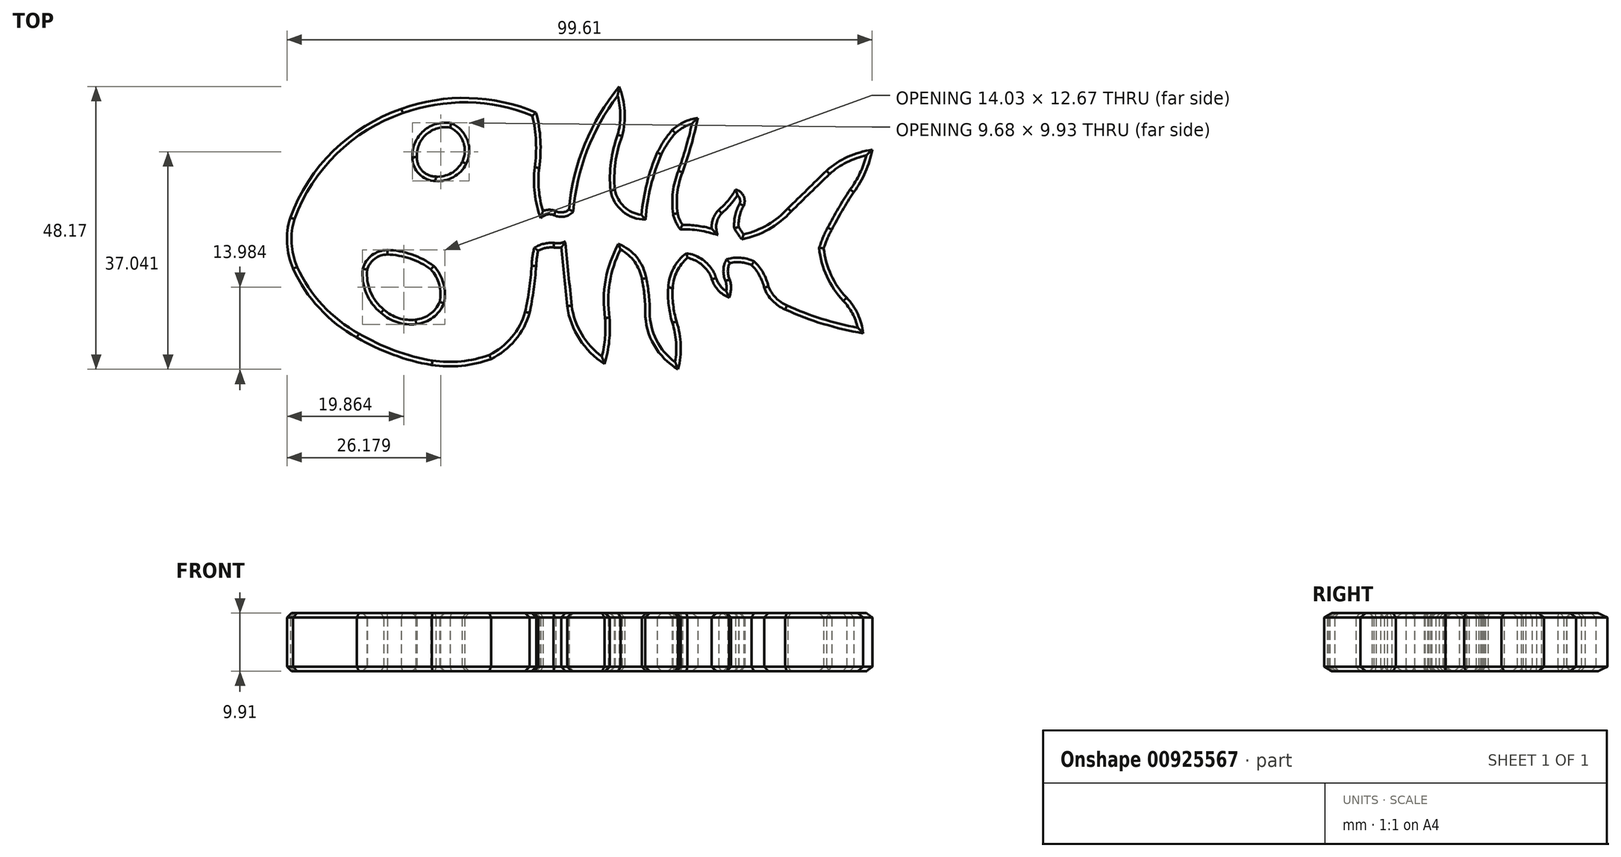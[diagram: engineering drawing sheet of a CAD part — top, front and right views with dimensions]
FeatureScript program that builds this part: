
annotation { "Feature Type Name" : "Feature", "Feature Type Description" : "" }
export const myFeature = defineFeature(function(context is Context, id is Id, definition is map)
    precondition{}
    {
        {
            var Q0;
            Q0=qCreatedBy(makeId("Top.planeOp"),FACE);
            var sketch = newSketch(context, id + "F0", { "sketchPlane" : qUnion([Q0])});
            skArc(sketch, "E0", {"start": v(-60.04, 23.84) * mm, "mid": v(-71.6, 16.74) * mm, "end": v(-78.96, 5.34) * mm});
            skArc(sketch, "E1", {"start": v(-37.1, 23.22) * mm, "mid": v(-48.52, 25.7) * mm, "end": v(-60.04, 23.84) * mm});
            skArc(sketch, "E2", {"start": v(-36.6, 13.8) * mm, "mid": v(-36.38, 18.53) * mm, "end": v(-37.1, 23.22) * mm});
            skArc(sketch, "E3", {"start": v(-36.6, 13.8) * mm, "mid": v(-36.65, 10.08) * mm, "end": v(-35.92, 6.44) * mm});
            skArc(sketch, "E4", {"start": v(-33.76, 6.44) * mm, "mid": v(-34.84, 6.66) * mm, "end": v(-35.92, 6.44) * mm});
            skArc(sketch, "E5", {"start": v(-33.76, 6.44) * mm, "mid": v(-32.6, 6.23) * mm, "end": v(-31.52, 6.72) * mm});
            skArc(sketch, "E6", {"start": v(-22.96, 27.66) * mm, "mid": v(-28.83, 17.84) * mm, "end": v(-31.52, 6.72) * mm});
            skArc(sketch, "E7", {"start": v(-22.49, 19.2) * mm, "mid": v(-22.03, 23.47) * mm, "end": v(-22.96, 27.66) * mm});
            skArc(sketch, "E8", {"start": v(-22.49, 19.2) * mm, "mid": v(-23.6, 14.71) * mm, "end": v(-23.7, 10.08) * mm});
            skArc(sketch, "E9", {"start": v(-23.7, 10.08) * mm, "mid": v(-22.13, 7.2) * mm, "end": v(-19.16, 5.8) * mm});
            skArc(sketch, "E10", {"start": v(-16.47, 16.41) * mm, "mid": v(-18.25, 11.21) * mm, "end": v(-19.16, 5.8) * mm});
            skArc(sketch, "E11", {"start": v(-13.94, 20.27) * mm, "mid": v(-15.34, 18.43) * mm, "end": v(-16.47, 16.41) * mm});
            skArc(sketch, "E12", {"start": v(-9.6, 22.32) * mm, "mid": v(-11.92, 21.61) * mm, "end": v(-13.94, 20.27) * mm});
            skArc(sketch, "E13", {"start": v(-12.2, 13.03) * mm, "mid": v(-10.72, 17.63) * mm, "end": v(-9.6, 22.32) * mm});
            skArc(sketch, "E14", {"start": v(-12.2, 13.03) * mm, "mid": v(-13.06, 9.6) * mm, "end": v(-13.04, 6.06) * mm});
            skArc(sketch, "E15", {"start": v(-13.04, 6.06) * mm, "mid": v(-12.7, 5.05) * mm, "end": v(-12.2, 4.12) * mm});
            skArc(sketch, "E16", {"start": v(-7.21, 3.46) * mm, "mid": v(-9.68, 3.95) * mm, "end": v(-12.2, 4.12) * mm});
            skArc(sketch, "E17", {"start": v(-6.05, 6.63) * mm, "mid": v(-6.97, 5.17) * mm, "end": v(-7.21, 3.46) * mm});
            skArc(sketch, "E18", {"start": v(-6.05, 6.63) * mm, "mid": v(-4.45, 8.24) * mm, "end": v(-3.16, 10.11) * mm});
            skArc(sketch, "E19", {"start": v(-1.78, 7.35) * mm, "mid": v(-1.82, 9.06) * mm, "end": v(-3.16, 10.11) * mm});
            skArc(sketch, "E20", {"start": v(-1.78, 7.35) * mm, "mid": v(-2.47, 5.6) * mm, "end": v(-2.63, 3.74) * mm});
            skArc(sketch, "E21", {"start": v(-2.63, 3.74) * mm, "mid": v(-2.22, 3.1) * mm, "end": v(-1.78, 2.48) * mm});
            skArc(sketch, "E22", {"start": v(-1.78, 2.48) * mm, "mid": v(2.33, 4.12) * mm, "end": v(5.75, 6.91) * mm});
            skArc(sketch, "E23", {"start": v(12.32, 13.31) * mm, "mid": v(9.03, 10.11) * mm, "end": v(5.75, 6.91) * mm});
            skArc(sketch, "E24", {"start": v(20.1, 16.9) * mm, "mid": v(15.95, 15.68) * mm, "end": v(12.32, 13.31) * mm});
            skArc(sketch, "E25", {"start": v(16.96, 9.67) * mm, "mid": v(18.94, 13.1) * mm, "end": v(20.1, 16.9) * mm});
            skArc(sketch, "E26", {"start": v(16.96, 9.67) * mm, "mid": v(15, 6.52) * mm, "end": v(13.2, 3.27) * mm});
            skArc(sketch, "E27", {"start": v(13.2, 3.27) * mm, "mid": v(12.44, 1.72) * mm, "end": v(11.85, 0.1) * mm});
            skArc(sketch, "E28", {"start": v(-49.69, 14.84) * mm, "mid": v(-49.5, 18.2) * mm, "end": v(-51.76, 20.68) * mm});
            skArc(sketch, "E29", {"start": v(-51.76, 20.68) * mm, "mid": v(-55.8, 19.5) * mm, "end": v(-57.41, 15.62) * mm});
            skArc(sketch, "E30", {"start": v(-57.41, 15.62) * mm, "mid": v(-56.48, 13.3) * mm, "end": v(-54.18, 12.33) * mm});
            skArc(sketch, "E31", {"start": v(-54.18, 12.33) * mm, "mid": v(-51.55, 12.9) * mm, "end": v(-49.69, 14.84) * mm});
            skArc(sketch, "E32", {"start": v(-53.52, -9.03) * mm, "mid": v(-53.61, -6.08) * mm, "end": v(-55.03, -3.48) * mm});
            skArc(sketch, "E33", {"start": v(-57.6, -12.05) * mm, "mid": v(-55.15, -11.1) * mm, "end": v(-53.52, -9.03) * mm});
            skArc(sketch, "E34", {"start": v(-63.02, -10.32) * mm, "mid": v(-60.5, -11.78) * mm, "end": v(-57.6, -12.05) * mm});
            skArc(sketch, "E35", {"start": v(-65.86, -3.53) * mm, "mid": v(-65.3, -7.28) * mm, "end": v(-63.02, -10.32) * mm});
            skArc(sketch, "E36", {"start": v(-62.44, -0.95) * mm, "mid": v(-64.58, -1.68) * mm, "end": v(-65.86, -3.53) * mm});
            skArc(sketch, "E37", {"start": v(-55.03, -3.48) * mm, "mid": v(-58.54, -1.65) * mm, "end": v(-62.44, -0.95) * mm});
            skArc(sketch, "E38", {"start": v(-78.96, 5.34) * mm, "mid": v(-79.48, 0.94) * mm, "end": v(-78.46, -3.36) * mm});
            skArc(sketch, "E39", {"start": v(-78.46, -3.36) * mm, "mid": v(-74, -10.1) * mm, "end": v(-67.63, -15.09) * mm});
            skArc(sketch, "E40", {"start": v(-67.63, -15.09) * mm, "mid": v(-61.46, -18) * mm, "end": v(-54.86, -19.79) * mm});
            skArc(sketch, "E41", {"start": v(-54.86, -19.79) * mm, "mid": v(-49.76, -19.9) * mm, "end": v(-44.78, -18.74) * mm});
            skArc(sketch, "E42", {"start": v(-44.78, -18.74) * mm, "mid": v(-40.67, -15.52) * mm, "end": v(-38.21, -10.9) * mm});
            skArc(sketch, "E43", {"start": v(-38.21, -10.9) * mm, "mid": v(-37.53, -6.93) * mm, "end": v(-37.1, -2.91) * mm});
            skArc(sketch, "E44", {"start": v(-36.76, -0.3) * mm, "mid": v(-36.99, -1.6) * mm, "end": v(-37.1, -2.91) * mm});
            skArc(sketch, "E45", {"start": v(-31.83, -9.75) * mm, "mid": v(-32.31, -4.75) * mm, "end": v(-32.8, 0.26) * mm});
            skArc(sketch, "E46", {"start": v(-34.14, 0.26) * mm, "mid": v(-33.47, 0.2) * mm, "end": v(-32.8, 0.26) * mm});
            skArc(sketch, "E47", {"start": v(-34.14, 0.26) * mm, "mid": v(-35.49, 0.16) * mm, "end": v(-36.76, -0.3) * mm});
            skArc(sketch, "E48", {"start": v(-31.83, -9.75) * mm, "mid": v(-29.73, -15.36) * mm, "end": v(-25.47, -19.58) * mm});
            skArc(sketch, "E49", {"start": v(-25.47, -19.58) * mm, "mid": v(-24.66, -15.68) * mm, "end": v(-24.61, -11.7) * mm});
            skArc(sketch, "E50", {"start": v(-22.75, -0.12) * mm, "mid": v(-24.6, -5.76) * mm, "end": v(-24.61, -11.7) * mm});
            skArc(sketch, "E51", {"start": v(-19.12, -5.13) * mm, "mid": v(-20.34, -2.2) * mm, "end": v(-22.75, -0.12) * mm});
            skArc(sketch, "E52", {"start": v(-18.53, -10.76) * mm, "mid": v(-18.67, -7.93) * mm, "end": v(-19.12, -5.13) * mm});
            skArc(sketch, "E53", {"start": v(-18.53, -10.76) * mm, "mid": v(-17.04, -16.4) * mm, "end": v(-12.93, -20.5) * mm});
            skArc(sketch, "E54", {"start": v(-12.93, -20.5) * mm, "mid": v(-12.5, -16.41) * mm, "end": v(-13.2, -12.35) * mm});
            skArc(sketch, "E55", {"start": v(-13.86, -6.63) * mm, "mid": v(-13.78, -9.52) * mm, "end": v(-13.2, -12.35) * mm});
            skArc(sketch, "E56", {"start": v(-11.33, -1.52) * mm, "mid": v(-13.13, -3.8) * mm, "end": v(-13.86, -6.63) * mm});
            skArc(sketch, "E57", {"start": v(-7.78, -3.92) * mm, "mid": v(-9.32, -2.37) * mm, "end": v(-11.33, -1.52) * mm});
            skArc(sketch, "E58", {"start": v(-7.21, -5.18) * mm, "mid": v(-6.08, -7.07) * mm, "end": v(-4.26, -8.3) * mm});
            skArc(sketch, "E59", {"start": v(-7.21, -5.18) * mm, "mid": v(-7.44, -4.53) * mm, "end": v(-7.78, -3.92) * mm});
            skArc(sketch, "E60", {"start": v(-4.26, -8.3) * mm, "mid": v(-3.94, -6.75) * mm, "end": v(-4.15, -5.18) * mm});
            skArc(sketch, "E61", {"start": v(-4.15, -2.4) * mm, "mid": v(-4.47, -3.8) * mm, "end": v(-4.15, -5.18) * mm});
            skArc(sketch, "E62", {"start": v(-0.43, -2.75) * mm, "mid": v(-2.26, -2.28) * mm, "end": v(-4.15, -2.4) * mm});
            skArc(sketch, "E63", {"start": v(1.7, -6.61) * mm, "mid": v(0.92, -4.53) * mm, "end": v(-0.43, -2.75) * mm});
            skArc(sketch, "E64", {"start": v(1.7, -6.61) * mm, "mid": v(3.12, -8.82) * mm, "end": v(5.28, -10.32) * mm});
            skArc(sketch, "E65", {"start": v(5.28, -10.32) * mm, "mid": v(11.79, -12.78) * mm, "end": v(18.56, -14.37) * mm});
            skArc(sketch, "E66", {"start": v(18.56, -14.37) * mm, "mid": v(17.65, -11.1) * mm, "end": v(15.73, -8.32) * mm});
            skArc(sketch, "E67", {"start": v(11.85, 0.1) * mm, "mid": v(13.1, -4.43) * mm, "end": v(15.73, -8.32) * mm});
            skSolve(sketch);
        }
        {
            var Q0;
            Q0=makeQuery(id+"F0.imprint","IMPRINT",FACE,{"disambiguationData":[TD([[makeQuery(id+"F0.imprint","IMPRINT",EDGE,{"derivedFrom":sQuery(id+"F0.wireOp",EDGE,"E0")}),1.0]])]});
            extrude(context, id + "F1", {"entities" : qUnion([Q0]), "depth" : 9.9 * mm, "offsetDistance" : 25.4 * mm});
        }
        {
            var Q0;
            Q0=makeQuery(id+"F1.opExtrude","CAP_FACE",FACE,{"disambiguationData":[OSD([sQuery(id+"F0.wireOp",EDGE,"E0"),sQuery(id+"F0.wireOp",EDGE,"E1"),sQuery(id+"F0.wireOp",EDGE,"E2"),sQuery(id+"F0.wireOp",EDGE,"E3"),sQuery(id+"F0.wireOp",EDGE,"E4"),sQuery(id+"F0.wireOp",EDGE,"E5"),sQuery(id+"F0.wireOp",EDGE,"E6"),sQuery(id+"F0.wireOp",EDGE,"E7"),sQuery(id+"F0.wireOp",EDGE,"E8"),sQuery(id+"F0.wireOp",EDGE,"E9"),sQuery(id+"F0.wireOp",EDGE,"E10"),sQuery(id+"F0.wireOp",EDGE,"E11"),sQuery(id+"F0.wireOp",EDGE,"E12"),sQuery(id+"F0.wireOp",EDGE,"E13"),sQuery(id+"F0.wireOp",EDGE,"E14"),sQuery(id+"F0.wireOp",EDGE,"E15"),sQuery(id+"F0.wireOp",EDGE,"E16"),sQuery(id+"F0.wireOp",EDGE,"E17"),sQuery(id+"F0.wireOp",EDGE,"E18"),sQuery(id+"F0.wireOp",EDGE,"E19"),sQuery(id+"F0.wireOp",EDGE,"E20"),sQuery(id+"F0.wireOp",EDGE,"E21"),sQuery(id+"F0.wireOp",EDGE,"E22"),sQuery(id+"F0.wireOp",EDGE,"E23"),sQuery(id+"F0.wireOp",EDGE,"E24"),sQuery(id+"F0.wireOp",EDGE,"E25"),sQuery(id+"F0.wireOp",EDGE,"E26"),sQuery(id+"F0.wireOp",EDGE,"E27"),sQuery(id+"F0.wireOp",EDGE,"E28"),sQuery(id+"F0.wireOp",EDGE,"E29"),sQuery(id+"F0.wireOp",EDGE,"E30"),sQuery(id+"F0.wireOp",EDGE,"E31"),sQuery(id+"F0.wireOp",EDGE,"E32"),sQuery(id+"F0.wireOp",EDGE,"E33"),sQuery(id+"F0.wireOp",EDGE,"E34"),sQuery(id+"F0.wireOp",EDGE,"E35"),sQuery(id+"F0.wireOp",EDGE,"E36"),sQuery(id+"F0.wireOp",EDGE,"E37"),sQuery(id+"F0.wireOp",EDGE,"E38"),sQuery(id+"F0.wireOp",EDGE,"E39"),sQuery(id+"F0.wireOp",EDGE,"E40"),sQuery(id+"F0.wireOp",EDGE,"E41"),sQuery(id+"F0.wireOp",EDGE,"E42"),sQuery(id+"F0.wireOp",EDGE,"E43"),sQuery(id+"F0.wireOp",EDGE,"E44"),sQuery(id+"F0.wireOp",EDGE,"E45"),sQuery(id+"F0.wireOp",EDGE,"E46"),sQuery(id+"F0.wireOp",EDGE,"E47"),sQuery(id+"F0.wireOp",EDGE,"E48"),sQuery(id+"F0.wireOp",EDGE,"E49"),sQuery(id+"F0.wireOp",EDGE,"E50"),sQuery(id+"F0.wireOp",EDGE,"E51"),sQuery(id+"F0.wireOp",EDGE,"E52"),sQuery(id+"F0.wireOp",EDGE,"E53"),sQuery(id+"F0.wireOp",EDGE,"E54"),sQuery(id+"F0.wireOp",EDGE,"E55"),sQuery(id+"F0.wireOp",EDGE,"E56"),sQuery(id+"F0.wireOp",EDGE,"E57"),sQuery(id+"F0.wireOp",EDGE,"E58"),sQuery(id+"F0.wireOp",EDGE,"E59"),sQuery(id+"F0.wireOp",EDGE,"E60"),sQuery(id+"F0.wireOp",EDGE,"E61"),sQuery(id+"F0.wireOp",EDGE,"E62"),sQuery(id+"F0.wireOp",EDGE,"E63"),sQuery(id+"F0.wireOp",EDGE,"E64"),sQuery(id+"F0.wireOp",EDGE,"E65"),sQuery(id+"F0.wireOp",EDGE,"E66"),sQuery(id+"F0.wireOp",EDGE,"E67")])],"isStart":false});
            var Q1;
            Q1=makeQuery(id+"F1.opExtrude","CAP_FACE",FACE,{"disambiguationData":[OSD([sQuery(id+"F0.wireOp",EDGE,"E0"),sQuery(id+"F0.wireOp",EDGE,"E1"),sQuery(id+"F0.wireOp",EDGE,"E2"),sQuery(id+"F0.wireOp",EDGE,"E3"),sQuery(id+"F0.wireOp",EDGE,"E4"),sQuery(id+"F0.wireOp",EDGE,"E5"),sQuery(id+"F0.wireOp",EDGE,"E6"),sQuery(id+"F0.wireOp",EDGE,"E7"),sQuery(id+"F0.wireOp",EDGE,"E8"),sQuery(id+"F0.wireOp",EDGE,"E9"),sQuery(id+"F0.wireOp",EDGE,"E10"),sQuery(id+"F0.wireOp",EDGE,"E11"),sQuery(id+"F0.wireOp",EDGE,"E12"),sQuery(id+"F0.wireOp",EDGE,"E13"),sQuery(id+"F0.wireOp",EDGE,"E14"),sQuery(id+"F0.wireOp",EDGE,"E15"),sQuery(id+"F0.wireOp",EDGE,"E16"),sQuery(id+"F0.wireOp",EDGE,"E17"),sQuery(id+"F0.wireOp",EDGE,"E18"),sQuery(id+"F0.wireOp",EDGE,"E19"),sQuery(id+"F0.wireOp",EDGE,"E20"),sQuery(id+"F0.wireOp",EDGE,"E21"),sQuery(id+"F0.wireOp",EDGE,"E22"),sQuery(id+"F0.wireOp",EDGE,"E23"),sQuery(id+"F0.wireOp",EDGE,"E24"),sQuery(id+"F0.wireOp",EDGE,"E25"),sQuery(id+"F0.wireOp",EDGE,"E26"),sQuery(id+"F0.wireOp",EDGE,"E27"),sQuery(id+"F0.wireOp",EDGE,"E28"),sQuery(id+"F0.wireOp",EDGE,"E29"),sQuery(id+"F0.wireOp",EDGE,"E30"),sQuery(id+"F0.wireOp",EDGE,"E31"),sQuery(id+"F0.wireOp",EDGE,"E32"),sQuery(id+"F0.wireOp",EDGE,"E33"),sQuery(id+"F0.wireOp",EDGE,"E34"),sQuery(id+"F0.wireOp",EDGE,"E35"),sQuery(id+"F0.wireOp",EDGE,"E36"),sQuery(id+"F0.wireOp",EDGE,"E37"),sQuery(id+"F0.wireOp",EDGE,"E38"),sQuery(id+"F0.wireOp",EDGE,"E39"),sQuery(id+"F0.wireOp",EDGE,"E40"),sQuery(id+"F0.wireOp",EDGE,"E41"),sQuery(id+"F0.wireOp",EDGE,"E42"),sQuery(id+"F0.wireOp",EDGE,"E43"),sQuery(id+"F0.wireOp",EDGE,"E44"),sQuery(id+"F0.wireOp",EDGE,"E45"),sQuery(id+"F0.wireOp",EDGE,"E46"),sQuery(id+"F0.wireOp",EDGE,"E47"),sQuery(id+"F0.wireOp",EDGE,"E48"),sQuery(id+"F0.wireOp",EDGE,"E49"),sQuery(id+"F0.wireOp",EDGE,"E50"),sQuery(id+"F0.wireOp",EDGE,"E51"),sQuery(id+"F0.wireOp",EDGE,"E52"),sQuery(id+"F0.wireOp",EDGE,"E53"),sQuery(id+"F0.wireOp",EDGE,"E54"),sQuery(id+"F0.wireOp",EDGE,"E55"),sQuery(id+"F0.wireOp",EDGE,"E56"),sQuery(id+"F0.wireOp",EDGE,"E57"),sQuery(id+"F0.wireOp",EDGE,"E58"),sQuery(id+"F0.wireOp",EDGE,"E59"),sQuery(id+"F0.wireOp",EDGE,"E60"),sQuery(id+"F0.wireOp",EDGE,"E61"),sQuery(id+"F0.wireOp",EDGE,"E62"),sQuery(id+"F0.wireOp",EDGE,"E63"),sQuery(id+"F0.wireOp",EDGE,"E64"),sQuery(id+"F0.wireOp",EDGE,"E65"),sQuery(id+"F0.wireOp",EDGE,"E66"),sQuery(id+"F0.wireOp",EDGE,"E67")])],"isStart":true});
            chamfer(context, id + "F2", {"entities" : qUnion([Q0, Q1]), "width" : 0.76 * mm, "tangentPropagation" : true});
        }
    });
